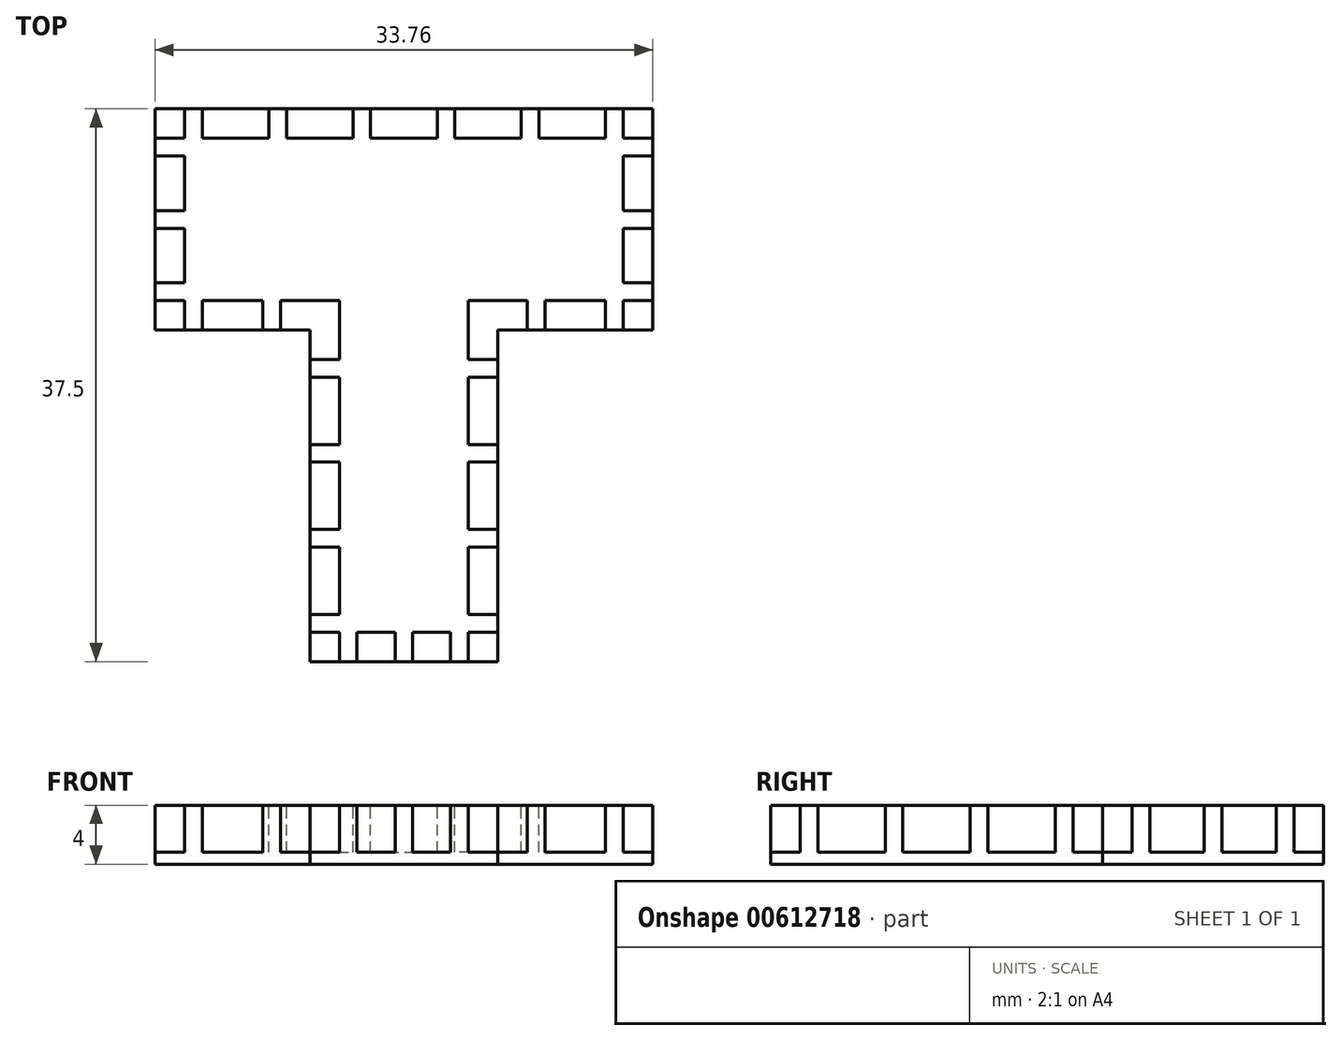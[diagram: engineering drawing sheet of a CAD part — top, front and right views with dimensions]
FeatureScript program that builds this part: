
annotation { "Feature Type Name" : "Feature", "Feature Type Description" : "" }
export const myFeature = defineFeature(function(context is Context, id is Id, definition is map)
    precondition{}
    {
        {
            var Q0;
            Q0=qCreatedBy(makeId("Top.planeOp"),FACE);
            var sketch = newSketch(context, id + "F0", { "sketchPlane" : qUnion([Q0])});
            skLineSegment(sketch, "E0", {"start": v(-6.38, 22.5) * mm, "end": v(-16.87, 22.5) * mm});
            skLineSegment(sketch, "E1", {"start": v(-16.87, 22.5) * mm, "end": v(-16.88, 37.5) * mm});
            skLineSegment(sketch, "E2", {"start": v(-16.88, 37.5) * mm, "end": v(16.88, 37.5) * mm});
            skLineSegment(sketch, "E3", {"start": v(16.88, 37.5) * mm, "end": v(16.87, 22.5) * mm});
            skLineSegment(sketch, "E4", {"start": v(16.87, 22.5) * mm, "end": v(6.37, 22.5) * mm});
            skLineSegment(sketch, "E5.top", {"start": v(-6.38, 0) * mm, "end": v(6.38, 0) * mm});
            skLineSegment(sketch, "E5.left", {"start": v(-6.38, 22.5) * mm, "end": v(-6.38, 0) * mm});
            skLineSegment(sketch, "E5.right", {"start": v(6.38, 22.5) * mm, "end": v(6.38, 0) * mm});
            skPoint(sketch, "E6.orphan", {"position": v(0, 22.5) * mm});
            skSolve(sketch);
        }
        {
            var Q0;
            Q0=qSketchRegion(id+"F0",true);
            extrude(context, id + "F1", {"entities" : qUnion([Q0]), "depth" : 4 * mm, "offsetDistance" : 25 * mm});
        }
        {
            var Q0;
            Q0=makeQuery(id+"F1.opExtrude","CAP_FACE",FACE,{"disambiguationData":[OSD([sQuery(id+"F0.wireOp",EDGE,"uOKdsRfc-QTFC-pgxs-Mzwl-pb8iHWvxuIRp"),sQuery(id+"F0.wireOp",EDGE,"E0"),sQuery(id+"F0.wireOp",EDGE,"E1"),sQuery(id+"F0.wireOp",EDGE,"E2"),sQuery(id+"F0.wireOp",EDGE,"E3"),sQuery(id+"F0.wireOp",EDGE,"E4"),sQuery(id+"F0.wireOp",EDGE,"Crn2ojsG-PLpP-f0Oz-MymE-scPMXzhO3pfo"),sQuery(id+"F0.wireOp",EDGE,"Z7oaMTb1-7bUf-fBLC-m8xH-oq2oitPBunsz")])],"isStart":false});
            var sketch = newSketch(context, id + "F2", { "sketchPlane" : qUnion([Q0])});
            skLineSegment(sketch, "E7.bottom", {"start": v(-13.67, 22.5) * mm, "end": v(-9.57, 22.5) * mm});
            skLineSegment(sketch, "E7.top", {"start": v(-13.67, 24.5) * mm, "end": v(-9.57, 24.5) * mm});
            skLineSegment(sketch, "E7.left", {"start": v(-13.67, 22.5) * mm, "end": v(-13.67, 24.5) * mm});
            skLineSegment(sketch, "E7.right", {"start": v(-9.57, 22.5) * mm, "end": v(-9.57, 24.5) * mm});
            skLineSegment(sketch, "E8.bottom", {"start": v(-16.87, 22.5) * mm, "end": v(-14.88, 22.5) * mm});
            skLineSegment(sketch, "E8.top", {"start": v(-16.88, 24.5) * mm, "end": v(-14.88, 24.5) * mm});
            skLineSegment(sketch, "E8.right", {"start": v(-14.88, 22.5) * mm, "end": v(-14.88, 24.5) * mm});
            skLineSegment(sketch, "E9.bottom", {"start": v(-16.88, 25.7) * mm, "end": v(-14.88, 25.7) * mm});
            skLineSegment(sketch, "E9.top", {"start": v(-16.88, 29.4) * mm, "end": v(-14.88, 29.4) * mm});
            skLineSegment(sketch, "E9.left", {"start": v(-16.87, 25.7) * mm, "end": v(-16.88, 29.4) * mm});
            skLineSegment(sketch, "E9.right", {"start": v(-14.87, 25.7) * mm, "end": v(-14.87, 29.4) * mm});
            skLineSegment(sketch, "E10.bottom", {"start": v(-16.88, 30.6) * mm, "end": v(-14.88, 30.6) * mm});
            skLineSegment(sketch, "E10.top", {"start": v(-16.88, 34.3) * mm, "end": v(-14.88, 34.3) * mm});
            skLineSegment(sketch, "E10.left", {"start": v(-16.87, 30.6) * mm, "end": v(-16.87, 34.3) * mm});
            skLineSegment(sketch, "E10.right", {"start": v(-14.88, 30.6) * mm, "end": v(-14.88, 34.3) * mm});
            skLineSegment(sketch, "E11.bottom", {"start": v(-13.67, 37.5) * mm, "end": v(-9.16, 37.5) * mm});
            skLineSegment(sketch, "E11.top", {"start": v(-13.67, 35.5) * mm, "end": v(-9.16, 35.5) * mm});
            skLineSegment(sketch, "E11.left", {"start": v(-13.67, 37.5) * mm, "end": v(-13.67, 35.5) * mm});
            skLineSegment(sketch, "E11.right", {"start": v(-9.16, 37.5) * mm, "end": v(-9.16, 35.5) * mm});
            skLineSegment(sketch, "E12.bottom", {"start": v(-7.96, 37.5) * mm, "end": v(-3.45, 37.5) * mm});
            skLineSegment(sketch, "E12.top", {"start": v(-7.96, 35.5) * mm, "end": v(-3.45, 35.5) * mm});
            skLineSegment(sketch, "E12.left", {"start": v(-7.96, 37.5) * mm, "end": v(-7.96, 35.5) * mm});
            skLineSegment(sketch, "E12.right", {"start": v(-3.45, 37.5) * mm, "end": v(-3.45, 35.5) * mm});
            skLineSegment(sketch, "E13.bottom", {"start": v(-2.25, 37.5) * mm, "end": v(0, 37.5) * mm});
            skLineSegment(sketch, "E13.top", {"start": v(-2.25, 35.5) * mm, "end": v(0, 35.5) * mm});
            skLineSegment(sketch, "E13.left", {"start": v(-2.25, 37.5) * mm, "end": v(-2.25, 35.5) * mm});
            skLineSegment(sketch, "E13.right", {"start": v(0, 37.5) * mm, "end": v(0, 35.5) * mm});
            skLineSegment(sketch, "E14.bottom", {"start": v(-16.88, 37.5) * mm, "end": v(-14.88, 37.5) * mm});
            skLineSegment(sketch, "E14.top", {"start": v(-16.88, 35.5) * mm, "end": v(-14.88, 35.5) * mm});
            skLineSegment(sketch, "E14.left", {"start": v(-16.88, 37.5) * mm, "end": v(-16.88, 35.5) * mm});
            skLineSegment(sketch, "E14.right", {"start": v(-14.88, 37.5) * mm, "end": v(-14.88, 35.5) * mm});
            skLineSegment(sketch, "E15.left", {"start": v(-16.88, 22.5) * mm, "end": v(-16.88, 24.5) * mm});
            skLineSegment(sketch, "E16.bottom", {"start": v(-6.38, 19.3) * mm, "end": v(-4.38, 19.3) * mm});
            skLineSegment(sketch, "E16.top", {"start": v(-6.37, 14.73) * mm, "end": v(-4.37, 14.73) * mm});
            skLineSegment(sketch, "E16.left", {"start": v(-6.37, 19.3) * mm, "end": v(-6.37, 14.73) * mm});
            skLineSegment(sketch, "E16.right", {"start": v(-4.38, 19.3) * mm, "end": v(-4.37, 14.73) * mm});
            skLineSegment(sketch, "E17.bottom", {"start": v(-6.38, 13.53) * mm, "end": v(-4.37, 13.53) * mm});
            skLineSegment(sketch, "E17.top", {"start": v(-6.37, 8.97) * mm, "end": v(-4.37, 8.97) * mm});
            skLineSegment(sketch, "E17.left", {"start": v(-6.37, 13.53) * mm, "end": v(-6.37, 8.97) * mm});
            skLineSegment(sketch, "E17.right", {"start": v(-4.37, 13.53) * mm, "end": v(-4.37, 8.97) * mm});
            skLineSegment(sketch, "E18.bottom", {"start": v(-6.38, 7.77) * mm, "end": v(-4.38, 7.77) * mm});
            skLineSegment(sketch, "E18.top", {"start": v(-6.37, 3.2) * mm, "end": v(-4.38, 3.2) * mm});
            skLineSegment(sketch, "E18.left", {"start": v(-6.37, 7.77) * mm, "end": v(-6.37, 3.2) * mm});
            skLineSegment(sketch, "E18.right", {"start": v(-4.38, 7.77) * mm, "end": v(-4.38, 3.2) * mm});
            skLineSegment(sketch, "E19.bottom", {"start": v(-6.38, 2) * mm, "end": v(-4.38, 2) * mm});
            skLineSegment(sketch, "E19.top", {"start": v(-6.37, 0) * mm, "end": v(-4.37, 0) * mm});
            skLineSegment(sketch, "E19.left", {"start": v(-6.38, 2) * mm, "end": v(-6.37, 0) * mm});
            skLineSegment(sketch, "E19.right", {"start": v(-4.38, 2) * mm, "end": v(-4.37, 0) * mm});
            skLineSegment(sketch, "E20.bottom", {"start": v(-3.17, 0) * mm, "end": v(0, 0) * mm});
            skLineSegment(sketch, "E20.top", {"start": v(-3.18, 2) * mm, "end": v(-0.6, 2) * mm});
            skLineSegment(sketch, "E20.left", {"start": v(-3.17, 0) * mm, "end": v(-3.18, 2) * mm});
            skLineSegment(sketch, "E20.right", {"start": v(-0.6, 0) * mm, "end": v(-0.6, 2) * mm});
            skPoint(sketch, "E21.orphan", {"position": v(0, 2) * mm});
            skLineSegment(sketch, "E22", {"start": v(-6.37, 22.5) * mm, "end": v(-6.37, 20.5) * mm});
            skLineSegment(sketch, "E23", {"start": v(-6.38, 20.5) * mm, "end": v(-4.37, 20.5) * mm});
            skLineSegment(sketch, "E24", {"start": v(-4.37, 20.5) * mm, "end": v(-4.37, 24.5) * mm});
            skLineSegment(sketch, "E25", {"start": v(-4.37, 24.5) * mm, "end": v(-8.37, 24.5) * mm});
            skLineSegment(sketch, "E26", {"start": v(-8.37, 24.5) * mm, "end": v(-8.37, 22.5) * mm});
            skLineSegment(sketch, "E27", {"start": v(-8.37, 22.5) * mm, "end": v(-6.38, 22.5) * mm});
            skSolve(sketch);
        }
        {
            var Q0;
            Q0=qSketchRegion(id+"F2",true);
            extrude(context, id + "F3", {"entities" : qUnion([Q0]), "oppositeDirection" : true, "depth" : 3.2 * mm, "offsetDistance" : 25 * mm});
        }
        {
            var Q0;
            Q0=makeQuery(id+"F3.opExtrude","SWEPT_BODY",BODY,{"disambiguationData":[OSD([sQuery(id+"F2.wireOp",EDGE,"E20.bottom"),sQuery(id+"F2.wireOp",EDGE,"E20.top"),sQuery(id+"F2.wireOp",EDGE,"E20.left"),sQuery(id+"F2.wireOp",EDGE,"E20.right")])]});
            var Q1;
            Q1=makeQuery(id+"F3.opExtrude","SWEPT_BODY",BODY,{"disambiguationData":[OSD([sQuery(id+"F2.wireOp",EDGE,"E19.bottom"),sQuery(id+"F2.wireOp",EDGE,"E19.top"),sQuery(id+"F2.wireOp",EDGE,"E19.left"),sQuery(id+"F2.wireOp",EDGE,"E19.right")])]});
            var Q2;
            Q2=makeQuery(id+"F3.opExtrude","SWEPT_BODY",BODY,{"disambiguationData":[OSD([sQuery(id+"F2.wireOp",EDGE,"E18.bottom"),sQuery(id+"F2.wireOp",EDGE,"E18.top"),sQuery(id+"F2.wireOp",EDGE,"E18.left"),sQuery(id+"F2.wireOp",EDGE,"E18.right")])]});
            var Q3;
            Q3=makeQuery(id+"F3.opExtrude","SWEPT_BODY",BODY,{"disambiguationData":[OSD([sQuery(id+"F2.wireOp",EDGE,"E17.bottom"),sQuery(id+"F2.wireOp",EDGE,"E17.top"),sQuery(id+"F2.wireOp",EDGE,"E17.left"),sQuery(id+"F2.wireOp",EDGE,"E17.right")])]});
            var Q4;
            Q4=makeQuery(id+"F3.opExtrude","SWEPT_BODY",BODY,{"disambiguationData":[OSD([sQuery(id+"F2.wireOp",EDGE,"E16.bottom"),sQuery(id+"F2.wireOp",EDGE,"E16.top"),sQuery(id+"F2.wireOp",EDGE,"E16.left"),sQuery(id+"F2.wireOp",EDGE,"E16.right")])]});
            var Q5;
            Q5=makeQuery(id+"F3.opExtrude","SWEPT_BODY",BODY,{"disambiguationData":[OSD([sQuery(id+"F2.wireOp",EDGE,"E7.bottom"),sQuery(id+"F2.wireOp",EDGE,"E7.top"),sQuery(id+"F2.wireOp",EDGE,"E7.left"),sQuery(id+"F2.wireOp",EDGE,"E7.right")])]});
            var Q6;
            Q6=makeQuery(id+"F3.opExtrude","SWEPT_BODY",BODY,{"disambiguationData":[OSD([sQuery(id+"F2.wireOp",EDGE,"E8.bottom"),sQuery(id+"F2.wireOp",EDGE,"E8.top"),sQuery(id+"F2.wireOp",EDGE,"E8.right"),sQuery(id+"F2.wireOp",EDGE,"E15.left")])]});
            var Q7;
            Q7=makeQuery(id+"F3.opExtrude","SWEPT_BODY",BODY,{"disambiguationData":[OSD([sQuery(id+"F2.wireOp",EDGE,"E9.bottom"),sQuery(id+"F2.wireOp",EDGE,"E9.top"),sQuery(id+"F2.wireOp",EDGE,"E9.left"),sQuery(id+"F2.wireOp",EDGE,"E9.right")])]});
            var Q8;
            Q8=makeQuery(id+"F3.opExtrude","SWEPT_BODY",BODY,{"disambiguationData":[OSD([sQuery(id+"F2.wireOp",EDGE,"E10.bottom"),sQuery(id+"F2.wireOp",EDGE,"E10.top"),sQuery(id+"F2.wireOp",EDGE,"E10.left"),sQuery(id+"F2.wireOp",EDGE,"E10.right")])]});
            var Q9;
            Q9=makeQuery(id+"F3.opExtrude","SWEPT_BODY",BODY,{"disambiguationData":[OSD([sQuery(id+"F2.wireOp",EDGE,"E14.bottom"),sQuery(id+"F2.wireOp",EDGE,"E14.top"),sQuery(id+"F2.wireOp",EDGE,"E14.left"),sQuery(id+"F2.wireOp",EDGE,"E14.right")])]});
            var Q10;
            Q10=makeQuery(id+"F3.opExtrude","SWEPT_BODY",BODY,{"disambiguationData":[OSD([sQuery(id+"F2.wireOp",EDGE,"E11.bottom"),sQuery(id+"F2.wireOp",EDGE,"E11.top"),sQuery(id+"F2.wireOp",EDGE,"E11.left"),sQuery(id+"F2.wireOp",EDGE,"E11.right")])]});
            var Q11;
            Q11=makeQuery(id+"F3.opExtrude","SWEPT_BODY",BODY,{"disambiguationData":[OSD([sQuery(id+"F2.wireOp",EDGE,"E12.bottom"),sQuery(id+"F2.wireOp",EDGE,"E12.top"),sQuery(id+"F2.wireOp",EDGE,"E12.left"),sQuery(id+"F2.wireOp",EDGE,"E12.right")])]});
            var Q12;
            Q12=makeQuery(id+"F3.opExtrude","SWEPT_BODY",BODY,{"disambiguationData":[OSD([sQuery(id+"F2.wireOp",EDGE,"E13.bottom"),sQuery(id+"F2.wireOp",EDGE,"E13.top"),sQuery(id+"F2.wireOp",EDGE,"E13.left"),sQuery(id+"F2.wireOp",EDGE,"E13.right")])]});
            var Q13;
            Q13=makeQuery(id+"F3.opExtrude","SWEPT_BODY",BODY,{"disambiguationData":[OSD([sQuery(id+"F2.wireOp",EDGE,"E22"),sQuery(id+"F2.wireOp",EDGE,"E23"),sQuery(id+"F2.wireOp",EDGE,"E24"),sQuery(id+"F2.wireOp",EDGE,"E25"),sQuery(id+"F2.wireOp",EDGE,"E26"),sQuery(id+"F2.wireOp",EDGE,"E27")])]});
            var Q14;
            Q14=qCreatedBy(makeId("Right.planeOp"),FACE);
            mirror(context, id + "F4", {"entities" : qUnion([Q0, Q1, Q2, Q3, Q4, Q5, Q6, Q7, Q8, Q9, Q10, Q11, Q12, Q13]), "mirrorPlane" : qUnion([Q14])});
        }
        {
            var Q0;
            Q0=makeQuery(id+"F3.opExtrude","SWEPT_BODY",BODY,{"disambiguationData":[OSD([sQuery(id+"F2.wireOp",EDGE,"E20.bottom"),sQuery(id+"F2.wireOp",EDGE,"E20.top"),sQuery(id+"F2.wireOp",EDGE,"E20.left"),sQuery(id+"F2.wireOp",EDGE,"E20.right")])]});
            var Q1;
            Q1=makeQuery(id+"F3.opExtrude","SWEPT_BODY",BODY,{"disambiguationData":[OSD([sQuery(id+"F2.wireOp",EDGE,"E19.bottom"),sQuery(id+"F2.wireOp",EDGE,"E19.top"),sQuery(id+"F2.wireOp",EDGE,"E19.left"),sQuery(id+"F2.wireOp",EDGE,"E19.right")])]});
            var Q2;
            Q2=makeQuery(id+"F3.opExtrude","SWEPT_BODY",BODY,{"disambiguationData":[OSD([sQuery(id+"F2.wireOp",EDGE,"E18.bottom"),sQuery(id+"F2.wireOp",EDGE,"E18.top"),sQuery(id+"F2.wireOp",EDGE,"E18.left"),sQuery(id+"F2.wireOp",EDGE,"E18.right")])]});
            var Q3;
            Q3=makeQuery(id+"F3.opExtrude","SWEPT_BODY",BODY,{"disambiguationData":[OSD([sQuery(id+"F2.wireOp",EDGE,"E17.bottom"),sQuery(id+"F2.wireOp",EDGE,"E17.top"),sQuery(id+"F2.wireOp",EDGE,"E17.left"),sQuery(id+"F2.wireOp",EDGE,"E17.right")])]});
            var Q4;
            Q4=makeQuery(id+"F3.opExtrude","SWEPT_BODY",BODY,{"disambiguationData":[OSD([sQuery(id+"F2.wireOp",EDGE,"E16.bottom"),sQuery(id+"F2.wireOp",EDGE,"E16.top"),sQuery(id+"F2.wireOp",EDGE,"E16.left"),sQuery(id+"F2.wireOp",EDGE,"E16.right")])]});
            var Q5;
            Q5=makeQuery(id+"F3.opExtrude","SWEPT_BODY",BODY,{"disambiguationData":[OSD([sQuery(id+"F2.wireOp",EDGE,"E7.bottom"),sQuery(id+"F2.wireOp",EDGE,"E7.top"),sQuery(id+"F2.wireOp",EDGE,"E7.left"),sQuery(id+"F2.wireOp",EDGE,"E7.right")])]});
            var Q6;
            Q6=makeQuery(id+"F3.opExtrude","SWEPT_BODY",BODY,{"disambiguationData":[OSD([sQuery(id+"F2.wireOp",EDGE,"E8.bottom"),sQuery(id+"F2.wireOp",EDGE,"E8.top"),sQuery(id+"F2.wireOp",EDGE,"E8.right"),sQuery(id+"F2.wireOp",EDGE,"E15.left")])]});
            var Q7;
            Q7=makeQuery(id+"F3.opExtrude","SWEPT_BODY",BODY,{"disambiguationData":[OSD([sQuery(id+"F2.wireOp",EDGE,"E9.bottom"),sQuery(id+"F2.wireOp",EDGE,"E9.top"),sQuery(id+"F2.wireOp",EDGE,"E9.left"),sQuery(id+"F2.wireOp",EDGE,"E9.right")])]});
            var Q8;
            Q8=makeQuery(id+"F3.opExtrude","SWEPT_BODY",BODY,{"disambiguationData":[OSD([sQuery(id+"F2.wireOp",EDGE,"E10.bottom"),sQuery(id+"F2.wireOp",EDGE,"E10.top"),sQuery(id+"F2.wireOp",EDGE,"E10.left"),sQuery(id+"F2.wireOp",EDGE,"E10.right")])]});
            var Q9;
            Q9=makeQuery(id+"F3.opExtrude","SWEPT_BODY",BODY,{"disambiguationData":[OSD([sQuery(id+"F2.wireOp",EDGE,"E14.bottom"),sQuery(id+"F2.wireOp",EDGE,"E14.top"),sQuery(id+"F2.wireOp",EDGE,"E14.left"),sQuery(id+"F2.wireOp",EDGE,"E14.right")])]});
            var Q10;
            Q10=makeQuery(id+"F3.opExtrude","SWEPT_BODY",BODY,{"disambiguationData":[OSD([sQuery(id+"F2.wireOp",EDGE,"E11.bottom"),sQuery(id+"F2.wireOp",EDGE,"E11.top"),sQuery(id+"F2.wireOp",EDGE,"E11.left"),sQuery(id+"F2.wireOp",EDGE,"E11.right")])]});
            var Q11;
            Q11=makeQuery(id+"F3.opExtrude","SWEPT_BODY",BODY,{"disambiguationData":[OSD([sQuery(id+"F2.wireOp",EDGE,"E12.bottom"),sQuery(id+"F2.wireOp",EDGE,"E12.top"),sQuery(id+"F2.wireOp",EDGE,"E12.left"),sQuery(id+"F2.wireOp",EDGE,"E12.right")])]});
            var Q12;
            Q12=makeQuery(id+"F3.opExtrude","SWEPT_BODY",BODY,{"disambiguationData":[OSD([sQuery(id+"F2.wireOp",EDGE,"E13.bottom"),sQuery(id+"F2.wireOp",EDGE,"E13.top"),sQuery(id+"F2.wireOp",EDGE,"E13.left"),sQuery(id+"F2.wireOp",EDGE,"E13.right")])]});
            var Q13;
            Q13=makeQuery(id+"F4.opPattern","COPY",BODY,{"derivedFrom":makeQuery(id+"F3.opExtrude","SWEPT_BODY",BODY,{"disambiguationData":[OSD([sQuery(id+"F2.wireOp",EDGE,"E13.bottom"),sQuery(id+"F2.wireOp",EDGE,"E13.top"),sQuery(id+"F2.wireOp",EDGE,"E13.left"),sQuery(id+"F2.wireOp",EDGE,"E13.right")])]}),"instanceName":"1"});
            var Q14;
            Q14=makeQuery(id+"F4.opPattern","COPY",BODY,{"derivedFrom":makeQuery(id+"F3.opExtrude","SWEPT_BODY",BODY,{"disambiguationData":[OSD([sQuery(id+"F2.wireOp",EDGE,"E12.bottom"),sQuery(id+"F2.wireOp",EDGE,"E12.top"),sQuery(id+"F2.wireOp",EDGE,"E12.left"),sQuery(id+"F2.wireOp",EDGE,"E12.right")])]}),"instanceName":"1"});
            var Q15;
            Q15=makeQuery(id+"F4.opPattern","COPY",BODY,{"derivedFrom":makeQuery(id+"F3.opExtrude","SWEPT_BODY",BODY,{"disambiguationData":[OSD([sQuery(id+"F2.wireOp",EDGE,"E11.bottom"),sQuery(id+"F2.wireOp",EDGE,"E11.top"),sQuery(id+"F2.wireOp",EDGE,"E11.left"),sQuery(id+"F2.wireOp",EDGE,"E11.right")])]}),"instanceName":"1"});
            var Q16;
            Q16=makeQuery(id+"F4.opPattern","COPY",BODY,{"derivedFrom":makeQuery(id+"F3.opExtrude","SWEPT_BODY",BODY,{"disambiguationData":[OSD([sQuery(id+"F2.wireOp",EDGE,"E14.bottom"),sQuery(id+"F2.wireOp",EDGE,"E14.top"),sQuery(id+"F2.wireOp",EDGE,"E14.left"),sQuery(id+"F2.wireOp",EDGE,"E14.right")])]}),"instanceName":"1"});
            var Q17;
            Q17=makeQuery(id+"F4.opPattern","COPY",BODY,{"derivedFrom":makeQuery(id+"F3.opExtrude","SWEPT_BODY",BODY,{"disambiguationData":[OSD([sQuery(id+"F2.wireOp",EDGE,"E10.bottom"),sQuery(id+"F2.wireOp",EDGE,"E10.top"),sQuery(id+"F2.wireOp",EDGE,"E10.left"),sQuery(id+"F2.wireOp",EDGE,"E10.right")])]}),"instanceName":"1"});
            var Q18;
            Q18=makeQuery(id+"F4.opPattern","COPY",BODY,{"derivedFrom":makeQuery(id+"F3.opExtrude","SWEPT_BODY",BODY,{"disambiguationData":[OSD([sQuery(id+"F2.wireOp",EDGE,"E9.bottom"),sQuery(id+"F2.wireOp",EDGE,"E9.top"),sQuery(id+"F2.wireOp",EDGE,"E9.left"),sQuery(id+"F2.wireOp",EDGE,"E9.right")])]}),"instanceName":"1"});
            var Q19;
            Q19=makeQuery(id+"F4.opPattern","COPY",BODY,{"derivedFrom":makeQuery(id+"F3.opExtrude","SWEPT_BODY",BODY,{"disambiguationData":[OSD([sQuery(id+"F2.wireOp",EDGE,"E8.bottom"),sQuery(id+"F2.wireOp",EDGE,"E8.top"),sQuery(id+"F2.wireOp",EDGE,"E8.right"),sQuery(id+"F2.wireOp",EDGE,"E15.left")])]}),"instanceName":"1"});
            var Q20;
            Q20=makeQuery(id+"F4.opPattern","COPY",BODY,{"derivedFrom":makeQuery(id+"F3.opExtrude","SWEPT_BODY",BODY,{"disambiguationData":[OSD([sQuery(id+"F2.wireOp",EDGE,"E7.bottom"),sQuery(id+"F2.wireOp",EDGE,"E7.top"),sQuery(id+"F2.wireOp",EDGE,"E7.left"),sQuery(id+"F2.wireOp",EDGE,"E7.right")])]}),"instanceName":"1"});
            var Q21;
            Q21=makeQuery(id+"F4.opPattern","COPY",BODY,{"derivedFrom":makeQuery(id+"F3.opExtrude","SWEPT_BODY",BODY,{"disambiguationData":[OSD([sQuery(id+"F2.wireOp",EDGE,"E16.bottom"),sQuery(id+"F2.wireOp",EDGE,"E16.top"),sQuery(id+"F2.wireOp",EDGE,"E16.left"),sQuery(id+"F2.wireOp",EDGE,"E16.right")])]}),"instanceName":"1"});
            var Q22;
            Q22=makeQuery(id+"F4.opPattern","COPY",BODY,{"derivedFrom":makeQuery(id+"F3.opExtrude","SWEPT_BODY",BODY,{"disambiguationData":[OSD([sQuery(id+"F2.wireOp",EDGE,"E17.bottom"),sQuery(id+"F2.wireOp",EDGE,"E17.top"),sQuery(id+"F2.wireOp",EDGE,"E17.left"),sQuery(id+"F2.wireOp",EDGE,"E17.right")])]}),"instanceName":"1"});
            var Q23;
            Q23=makeQuery(id+"F4.opPattern","COPY",BODY,{"derivedFrom":makeQuery(id+"F3.opExtrude","SWEPT_BODY",BODY,{"disambiguationData":[OSD([sQuery(id+"F2.wireOp",EDGE,"E18.bottom"),sQuery(id+"F2.wireOp",EDGE,"E18.top"),sQuery(id+"F2.wireOp",EDGE,"E18.left"),sQuery(id+"F2.wireOp",EDGE,"E18.right")])]}),"instanceName":"1"});
            var Q24;
            Q24=makeQuery(id+"F4.opPattern","COPY",BODY,{"derivedFrom":makeQuery(id+"F3.opExtrude","SWEPT_BODY",BODY,{"disambiguationData":[OSD([sQuery(id+"F2.wireOp",EDGE,"E19.bottom"),sQuery(id+"F2.wireOp",EDGE,"E19.top"),sQuery(id+"F2.wireOp",EDGE,"E19.left"),sQuery(id+"F2.wireOp",EDGE,"E19.right")])]}),"instanceName":"1"});
            var Q25;
            Q25=makeQuery(id+"F4.opPattern","COPY",BODY,{"derivedFrom":makeQuery(id+"F3.opExtrude","SWEPT_BODY",BODY,{"disambiguationData":[OSD([sQuery(id+"F2.wireOp",EDGE,"E20.bottom"),sQuery(id+"F2.wireOp",EDGE,"E20.top"),sQuery(id+"F2.wireOp",EDGE,"E20.left"),sQuery(id+"F2.wireOp",EDGE,"E20.right")])]}),"instanceName":"1"});
            var Q26;
            Q26=makeQuery(id+"F3.opExtrude","SWEPT_BODY",BODY,{"disambiguationData":[OSD([sQuery(id+"F2.wireOp",EDGE,"JUDqh6x8-p85M-dCCK-uQO0-KAEB9dgT3CNB.bottom"),sQuery(id+"F2.wireOp",EDGE,"JUDqh6x8-p85M-dCCK-uQO0-KAEB9dgT3CNB.top"),sQuery(id+"F2.wireOp",EDGE,"JUDqh6x8-p85M-dCCK-uQO0-KAEB9dgT3CNB.left"),sQuery(id+"F2.wireOp",EDGE,"JUDqh6x8-p85M-dCCK-uQO0-KAEB9dgT3CNB.right")])]});
            var Q27;
            Q27=makeQuery(id+"F3.opExtrude","SWEPT_BODY",BODY,{"disambiguationData":[OSD([sQuery(id+"F2.wireOp",EDGE,"E22"),sQuery(id+"F2.wireOp",EDGE,"E23"),sQuery(id+"F2.wireOp",EDGE,"E24"),sQuery(id+"F2.wireOp",EDGE,"E25"),sQuery(id+"F2.wireOp",EDGE,"E26"),sQuery(id+"F2.wireOp",EDGE,"E27")])]});
            var Q28;
            Q28=makeQuery(id+"F4.opPattern","COPY",BODY,{"derivedFrom":makeQuery(id+"F3.opExtrude","SWEPT_BODY",BODY,{"disambiguationData":[OSD([sQuery(id+"F2.wireOp",EDGE,"E22"),sQuery(id+"F2.wireOp",EDGE,"E23"),sQuery(id+"F2.wireOp",EDGE,"E24"),sQuery(id+"F2.wireOp",EDGE,"E25"),sQuery(id+"F2.wireOp",EDGE,"E26"),sQuery(id+"F2.wireOp",EDGE,"E27")])]}),"instanceName":"1"});
            var Q29;
            Q29=makeQuery(id+"F1.opExtrude","SWEPT_BODY",BODY,{"disambiguationData":[OSD([sQuery(id+"F0.wireOp",EDGE,"uOKdsRfc-QTFC-pgxs-Mzwl-pb8iHWvxuIRp"),sQuery(id+"F0.wireOp",EDGE,"E0"),sQuery(id+"F0.wireOp",EDGE,"E1"),sQuery(id+"F0.wireOp",EDGE,"E2"),sQuery(id+"F0.wireOp",EDGE,"E3"),sQuery(id+"F0.wireOp",EDGE,"E4"),sQuery(id+"F0.wireOp",EDGE,"Crn2ojsG-PLpP-f0Oz-MymE-scPMXzhO3pfo"),sQuery(id+"F0.wireOp",EDGE,"Z7oaMTb1-7bUf-fBLC-m8xH-oq2oitPBunsz")])]});
            booleanBodies(context, id + "F5", {"operationType" : BooleanOperationType.SUBTRACTION, "tools" : qUnion([Q0, Q1, Q2, Q3, Q4, Q5, Q6, Q7, Q8, Q9, Q10, Q11, Q12, Q13, Q14, Q15, Q16, Q17, Q18, Q19, Q20, Q21, Q22, Q23, Q24, Q25, Q26, Q27, Q28]), "targets" : qUnion([Q29])});
        }
    });
